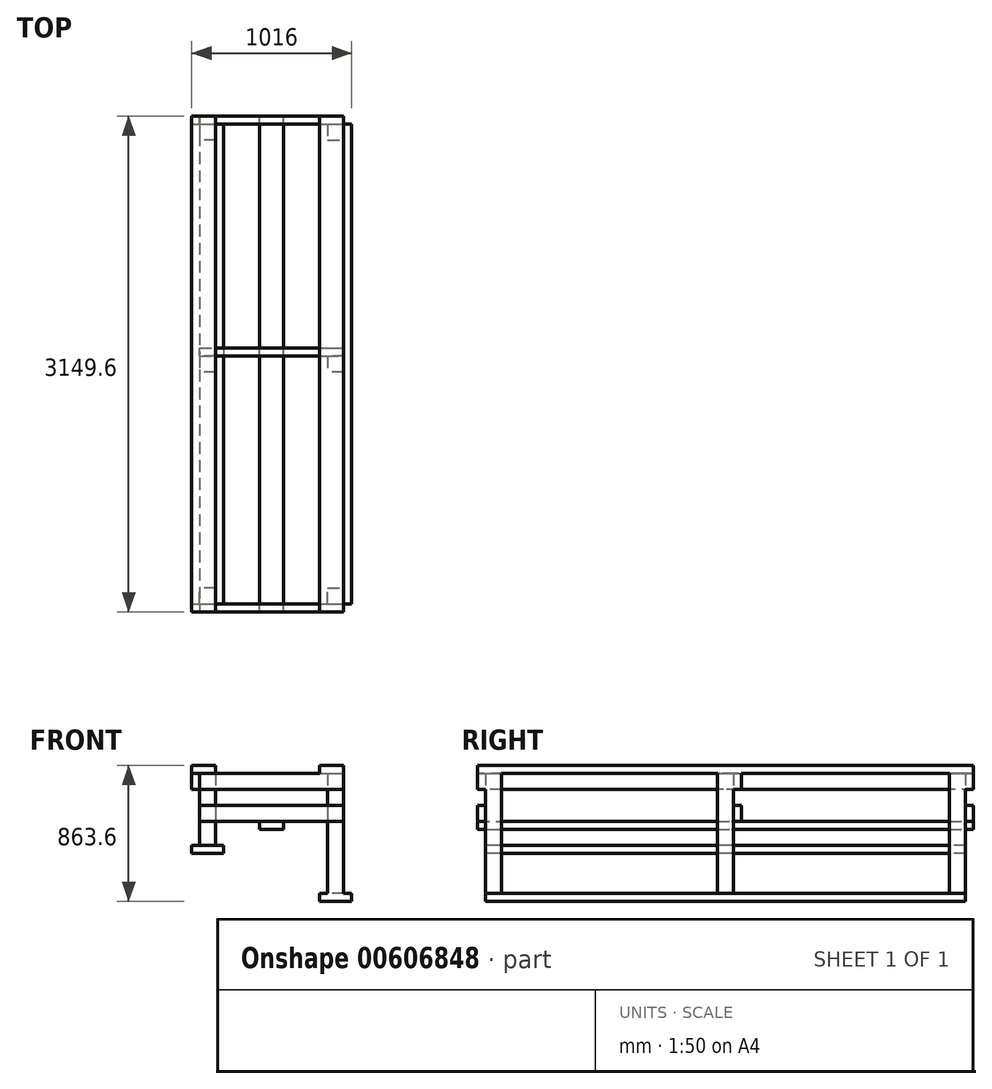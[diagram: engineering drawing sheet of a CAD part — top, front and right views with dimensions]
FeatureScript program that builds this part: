
annotation { "Feature Type Name" : "Feature", "Feature Type Description" : "" }
export const myFeature = defineFeature(function(context is Context, id is Id, definition is map)
    precondition{}
    {
        {
            var Q0;
            Q0=qCreatedBy(makeId("Front.planeOp"),FACE);
            var sketch = newSketch(context, id + "F0", { "sketchPlane" : qUnion([Q0])});
            skLineSegment(sketch, "E0.bottom", {"start": v(0, 0) * mm, "end": v(203.2, 0) * mm});
            skLineSegment(sketch, "E0.top", {"start": v(0, 50.8) * mm, "end": v(203.2, 50.8) * mm});
            skLineSegment(sketch, "E0.left", {"start": v(0, 0) * mm, "end": v(0, 50.8) * mm});
            skLineSegment(sketch, "E0.right", {"start": v(203.2, 0) * mm, "end": v(203.2, 50.8) * mm});
            skSolve(sketch);
        }
        {
            var Q0;
            Q0=makeQuery(id+"F0.imprint","IMPRINT",FACE,{"disambiguationData":[TD([[makeQuery(id+"F0.imprint","IMPRINT",EDGE,{"derivedFrom":sQuery(id+"F0.wireOp",EDGE,"E0.bottom")}),1.0]])]});
            extrude(context, id + "F1", {"entities" : qUnion([Q0]), "depth" : 3048 * mm, "offsetDistance" : 25.4 * mm});
        }
        {
            var Q0;
            Q0=makeQuery(id+"F1.opExtrude","SWEPT_FACE",FACE,{"disambiguationData":[OSD([sQuery(id+"F0.wireOp",EDGE,"E0.top")])]});
            var sketch = newSketch(context, id + "F2", { "sketchPlane" : qUnion([Q0])});
            skLineSegment(sketch, "E1", {"start": v(0, -3048) * mm, "end": v(50.8, -3048) * mm});
            skLineSegment(sketch, "E2.bottom", {"start": v(50.8, -3048) * mm, "end": v(152.4, -3048) * mm});
            skLineSegment(sketch, "E2.top", {"start": v(50.8, -2946.4) * mm, "end": v(152.4, -2946.4) * mm});
            skLineSegment(sketch, "E2.left", {"start": v(50.8, -3048) * mm, "end": v(50.8, -2946.4) * mm});
            skLineSegment(sketch, "E2.right", {"start": v(152.4, -3048) * mm, "end": v(152.4, -2946.4) * mm});
            skLineSegment(sketch, "E3", {"start": v(0, -3048) * mm, "end": v(0, -1524) * mm});
            skLineSegment(sketch, "E4", {"start": v(0, -1524) * mm, "end": v(203.2, -1524) * mm});
            skLineSegment(sketch, "E5.bottom", {"start": v(152.4, -1473.2) * mm, "end": v(50.8, -1473.2) * mm});
            skLineSegment(sketch, "E5.top", {"start": v(152.4, -1574.8) * mm, "end": v(50.8, -1574.8) * mm});
            skLineSegment(sketch, "E5.left", {"start": v(152.4, -1473.2) * mm, "end": v(152.4, -1574.8) * mm});
            skLineSegment(sketch, "E5.right", {"start": v(50.8, -1473.2) * mm, "end": v(50.8, -1574.8) * mm});
            skPoint(sketch, "E5.middle", {"position": v(101.6, -1524) * mm});
            skLineSegment(sketch, "E6", {"start": v(0, 0) * mm, "end": v(50.8, 0) * mm});
            skLineSegment(sketch, "E7.bottom", {"start": v(50.8, 0) * mm, "end": v(152.4, 0) * mm});
            skLineSegment(sketch, "E7.top", {"start": v(50.8, -101.6) * mm, "end": v(152.4, -101.6) * mm});
            skLineSegment(sketch, "E7.left", {"start": v(50.8, 0) * mm, "end": v(50.8, -101.6) * mm});
            skLineSegment(sketch, "E7.right", {"start": v(152.4, 0) * mm, "end": v(152.4, -101.6) * mm});
            skSolve(sketch);
        }
        {
            var Q0;
            Q0=makeQuery(id+"F2.imprint","IMPRINT",FACE,{"disambiguationData":[TD([[makeQuery(id+"F2.imprint","IMPRINT",EDGE,{"derivedFrom":sQuery(id+"F2.wireOp",EDGE,"E2.bottom")}),1.0]])]});
            var Q1;
            {var subQ5=sQuery(id+"F2.wireOp",EDGE,"E5.top");Q1=makeQuery(id+"F2.imprint","IMPRINT",FACE,{"disambiguationData":[TD([[makeQuery(id+"F2.imprint","IMPRINT",EDGE,{"derivedFrom":subQ5}),-1.0]])]});}
            var Q2;
            {var subQ5=sQuery(id+"F2.wireOp",EDGE,"E5.bottom");Q2=makeQuery(id+"F2.imprint","IMPRINT",FACE,{"disambiguationData":[TD([[makeQuery(id+"F2.imprint","IMPRINT",EDGE,{"derivedFrom":subQ5}),1.0]])]});}
            var Q3;
            Q3=makeQuery(id+"F2.imprint","IMPRINT",FACE,{"disambiguationData":[TD([[makeQuery(id+"F2.imprint","IMPRINT",EDGE,{"derivedFrom":sQuery(id+"F2.wireOp",EDGE,"E7.bottom")}),-1.0]])]});
            extrude(context, id + "F3", {"entities" : qUnion([Q0, Q1, Q2, Q3]), "operationType" : NewBodyOperationType.ADD, "depth" : 762 * mm, "offsetDistance" : 25.4 * mm});
        }
        {
            var Q0;
            Q0=makeQuery(id+"F3.opExtrude","SWEPT_FACE",FACE,{"disambiguationData":[OSD([sQuery(id+"F2.wireOp",EDGE,"E7.right")])]});
            var sketch = newSketch(context, id + "F4", { "sketchPlane" : qUnion([Q0])});
            skLineSegment(sketch, "E8.bottom", {"start": v(0, 812.8) * mm, "end": v(50.8, 812.8) * mm});
            skLineSegment(sketch, "E8.top", {"start": v(0, 711.2) * mm, "end": v(50.8, 711.2) * mm});
            skLineSegment(sketch, "E8.left", {"start": v(0, 812.8) * mm, "end": v(0, 711.2) * mm});
            skLineSegment(sketch, "E8.right", {"start": v(50.8, 812.8) * mm, "end": v(50.8, 711.2) * mm});
            skSolve(sketch);
        }
        {
            var Q0;
            Q0=makeQuery(id+"F4.imprint","IMPRINT",FACE,{"disambiguationData":[TD([[makeQuery(id+"F4.imprint","IMPRINT",EDGE,{"derivedFrom":sQuery(id+"F4.wireOp",EDGE,"E8.bottom")}),-1.0]])]});
            extrude(context, id + "F5", {"entities" : qUnion([Q0]), "operationType" : NewBodyOperationType.ADD, "oppositeDirection" : true, "depth" : 914.4 * mm, "offsetDistance" : 25.4 * mm});
        }
        {
            var Q0;
            Q0=makeQuery(id+"F3.opExtrude","SWEPT_FACE",FACE,{"disambiguationData":[OSD([sQuery(id+"F2.wireOp",EDGE,"E2.right")])]});
            var sketch = newSketch(context, id + "F6", { "sketchPlane" : qUnion([Q0])});
            skLineSegment(sketch, "E9.bottom", {"start": v(-3048, 812.8) * mm, "end": v(-3098.8, 812.8) * mm});
            skLineSegment(sketch, "E9.top", {"start": v(-3048, 711.2) * mm, "end": v(-3098.8, 711.2) * mm});
            skLineSegment(sketch, "E9.left", {"start": v(-3048, 812.8) * mm, "end": v(-3048, 711.2) * mm});
            skLineSegment(sketch, "E9.right", {"start": v(-3098.8, 812.8) * mm, "end": v(-3098.8, 711.2) * mm});
            skSolve(sketch);
        }
        {
            var Q0;
            Q0=makeQuery(id+"F6.imprint","IMPRINT",FACE,{"disambiguationData":[TD([[makeQuery(id+"F6.imprint","IMPRINT",EDGE,{"derivedFrom":sQuery(id+"F6.wireOp",EDGE,"E9.bottom")}),1.0]])]});
            extrude(context, id + "F7", {"entities" : qUnion([Q0]), "operationType" : NewBodyOperationType.ADD, "oppositeDirection" : true, "depth" : 914.4 * mm, "offsetDistance" : 25.4 * mm});
        }
        {
            var Q0;
            Q0=makeQuery(id+"F3.opExtrude","SWEPT_FACE",FACE,{"disambiguationData":[OSD([sQuery(id+"F2.wireOp",EDGE,"E5.left")])]});
            var sketch = newSketch(context, id + "F8", { "sketchPlane" : qUnion([Q0])});
            skLineSegment(sketch, "E10.bottom", {"start": v(-1473.2, 812.8) * mm, "end": v(-1422.4, 812.8) * mm});
            skLineSegment(sketch, "E10.top", {"start": v(-1473.2, 711.2) * mm, "end": v(-1422.4, 711.2) * mm});
            skLineSegment(sketch, "E10.left", {"start": v(-1473.2, 812.8) * mm, "end": v(-1473.2, 711.2) * mm});
            skLineSegment(sketch, "E10.right", {"start": v(-1422.4, 812.8) * mm, "end": v(-1422.4, 711.2) * mm});
            skSolve(sketch);
        }
        {
            var Q0;
            Q0=makeQuery(id+"F8.imprint","IMPRINT",FACE,{"disambiguationData":[TD([[makeQuery(id+"F8.imprint","IMPRINT",EDGE,{"derivedFrom":sQuery(id+"F8.wireOp",EDGE,"E10.bottom")}),-1.0]])]});
            extrude(context, id + "F9", {"entities" : qUnion([Q0]), "operationType" : NewBodyOperationType.ADD, "oppositeDirection" : true, "depth" : 914.4 * mm, "offsetDistance" : 25.4 * mm});
        }
        {
            var Q0;
            Q0=makeQuery(id+"F7.opExtrude","CAP_FACE",FACE,{"disambiguationData":[OSD([sQuery(id+"F6.wireOp",EDGE,"E9.bottom"),sQuery(id+"F6.wireOp",EDGE,"E9.top"),sQuery(id+"F6.wireOp",EDGE,"E9.left"),sQuery(id+"F6.wireOp",EDGE,"E9.right")])],"isStart":false});
            var sketch = newSketch(context, id + "F10", { "sketchPlane" : qUnion([Q0])});
            skLineSegment(sketch, "E11.bottom", {"start": v(3048, 812.8) * mm, "end": v(2946.4, 812.8) * mm});
            skLineSegment(sketch, "E11.top", {"start": v(3048, 355.6) * mm, "end": v(2946.4, 355.6) * mm});
            skLineSegment(sketch, "E11.left", {"start": v(3048, 812.8) * mm, "end": v(3048, 355.6) * mm});
            skLineSegment(sketch, "E11.right", {"start": v(2946.4, 812.8) * mm, "end": v(2946.4, 355.6) * mm});
            skSolve(sketch);
        }
        {
            var Q0;
            Q0=makeQuery(id+"F5.opExtrude","CAP_FACE",FACE,{"disambiguationData":[OSD([sQuery(id+"F4.wireOp",EDGE,"E8.bottom"),sQuery(id+"F4.wireOp",EDGE,"E8.top"),sQuery(id+"F4.wireOp",EDGE,"E8.left"),sQuery(id+"F4.wireOp",EDGE,"E8.right")])],"isStart":false});
            var sketch = newSketch(context, id + "F11", { "sketchPlane" : qUnion([Q0])});
            skLineSegment(sketch, "E12.bottom", {"start": v(0, 812.8) * mm, "end": v(101.6, 812.8) * mm});
            skLineSegment(sketch, "E12.top", {"start": v(0, 355.6) * mm, "end": v(101.6, 355.6) * mm});
            skLineSegment(sketch, "E12.left", {"start": v(0, 812.8) * mm, "end": v(0, 355.6) * mm});
            skLineSegment(sketch, "E12.right", {"start": v(101.6, 812.8) * mm, "end": v(101.6, 355.6) * mm});
            skSolve(sketch);
        }
        {
            var Q0;
            Q0=makeQuery(id+"F9.opExtrude","CAP_FACE",FACE,{"disambiguationData":[OSD([sQuery(id+"F8.wireOp",EDGE,"E10.bottom"),sQuery(id+"F8.wireOp",EDGE,"E10.top"),sQuery(id+"F8.wireOp",EDGE,"E10.left"),sQuery(id+"F8.wireOp",EDGE,"E10.right")])],"isStart":false});
            var sketch = newSketch(context, id + "F12", { "sketchPlane" : qUnion([Q0])});
            skLineSegment(sketch, "E13.bottom", {"start": v(1473.2, 812.8) * mm, "end": v(1574.8, 812.8) * mm});
            skLineSegment(sketch, "E13.top", {"start": v(1473.2, 355.6) * mm, "end": v(1574.8, 355.6) * mm});
            skLineSegment(sketch, "E13.left", {"start": v(1473.2, 812.8) * mm, "end": v(1473.2, 355.6) * mm});
            skLineSegment(sketch, "E13.right", {"start": v(1574.8, 812.8) * mm, "end": v(1574.8, 355.6) * mm});
            skSolve(sketch);
        }
        {
            var Q0;
            {var subQ1=sQuery(id+"F10.wireOp",EDGE,"E11.bottom");Q0=makeQuery(id+"F10.imprint","IMPRINT",FACE,{"disambiguationData":[TD([[makeQuery(id+"F10.imprint","IMPRINT",EDGE,{"derivedFrom":subQ1}),1.0]])]});}
            var Q1;
            {var subQ1=sQuery(id+"F12.wireOp",EDGE,"E13.bottom");Q1=makeQuery(id+"F12.imprint","IMPRINT",FACE,{"disambiguationData":[TD([[makeQuery(id+"F12.imprint","IMPRINT",EDGE,{"derivedFrom":subQ1}),-1.0]])]});}
            var Q2;
            {var subQ1=sQuery(id+"F11.wireOp",EDGE,"E12.bottom");Q2=makeQuery(id+"F11.imprint","IMPRINT",FACE,{"disambiguationData":[TD([[makeQuery(id+"F11.imprint","IMPRINT",EDGE,{"derivedFrom":subQ1}),-1.0]])]});}
            extrude(context, id + "F13", {"entities" : qUnion([Q0, Q1, Q2]), "oppositeDirection" : true, "depth" : 101.6 * mm, "offsetDistance" : 25.4 * mm});
        }
        {
            var Q0;
            Q0=makeQuery(id+"F7.opExtrude","SWEPT_FACE",FACE,{"disambiguationData":[OSD([sQuery(id+"F6.wireOp",EDGE,"E9.right")])]});
            var sketch = newSketch(context, id + "F14", { "sketchPlane" : qUnion([Q0])});
            skLineSegment(sketch, "E14.bottom", {"start": v(-762, 812.8) * mm, "end": v(-812.8, 812.8) * mm});
            skLineSegment(sketch, "E14.top", {"start": v(-762, 711.2) * mm, "end": v(-812.8, 711.2) * mm});
            skLineSegment(sketch, "E14.left", {"start": v(-762, 812.8) * mm, "end": v(-762, 711.2) * mm});
            skLineSegment(sketch, "E14.right", {"start": v(-812.8, 812.8) * mm, "end": v(-812.8, 711.2) * mm});
            skSolve(sketch);
        }
        {
            var Q0;
            Q0=makeQuery(id+"F14.imprint","IMPRINT",FACE,{"disambiguationData":[TD([[makeQuery(id+"F14.imprint","IMPRINT",EDGE,{"derivedFrom":sQuery(id+"F14.wireOp",EDGE,"E14.bottom")}),1.0]])]});
            extrude(context, id + "F15", {"entities" : qUnion([Q0]), "oppositeDirection" : true, "depth" : 3149.6 * mm, "offsetDistance" : 25.4 * mm});
        }
        {
            var Q0;
            Q0=makeQuery(id+"F13.opExtrude","SWEPT_FACE",FACE,{"disambiguationData":[OSD([sQuery(id+"F10.wireOp",EDGE,"E11.left")])]});
            var sketch = newSketch(context, id + "F16", { "sketchPlane" : qUnion([Q0])});
            skLineSegment(sketch, "E15", {"start": v(-660.4, 355.6) * mm, "end": v(-609.6, 355.6) * mm});
            skLineSegment(sketch, "E16.bottom", {"start": v(-609.6, 355.6) * mm, "end": v(-812.8, 355.6) * mm});
            skLineSegment(sketch, "E16.top", {"start": v(-609.6, 304.8) * mm, "end": v(-812.8, 304.8) * mm});
            skLineSegment(sketch, "E16.left", {"start": v(-609.6, 355.6) * mm, "end": v(-609.6, 304.8) * mm});
            skLineSegment(sketch, "E16.right", {"start": v(-812.8, 355.6) * mm, "end": v(-812.8, 304.8) * mm});
            skSolve(sketch);
        }
        {
            var Q0;
            Q0=makeQuery(id+"F16.imprint","IMPRINT",FACE,{"disambiguationData":[TD([[makeQuery(id+"F16.imprint","IMPRINT",EDGE,{"derivedFrom":sQuery(id+"F16.wireOp",EDGE,"E16.top")}),-1.0]])]});
            extrude(context, id + "F17", {"entities" : qUnion([Q0]), "oppositeDirection" : true, "depth" : 3048 * mm, "offsetDistance" : 25.4 * mm});
        }
        {
            var Q0;
            Q0=makeQuery(id+"F5.boolean.opBoolean","MERGE",FACE,{"derivedFrom":[makeQuery(id+"F3.opExtrude","SWEPT_FACE",FACE,{"disambiguationData":[OSD([sQuery(id+"F2.wireOp",EDGE,"E7.right")])]}),makeQuery(id+"F5.opExtrude","CAP_FACE",FACE,{"disambiguationData":[OSD([sQuery(id+"F4.wireOp",EDGE,"E8.bottom"),sQuery(id+"F4.wireOp",EDGE,"E8.top"),sQuery(id+"F4.wireOp",EDGE,"E8.left"),sQuery(id+"F4.wireOp",EDGE,"E8.right")])],"isStart":true})]});
            var sketch = newSketch(context, id + "F18", { "sketchPlane" : qUnion([Q0])});
            skLineSegment(sketch, "E17", {"start": v(0, 711.2) * mm, "end": v(0, 609.6) * mm});
            skLineSegment(sketch, "E18.bottom", {"start": v(0, 609.6) * mm, "end": v(50.8, 609.6) * mm});
            skLineSegment(sketch, "E18.top", {"start": v(0, 508) * mm, "end": v(50.8, 508) * mm});
            skLineSegment(sketch, "E18.left", {"start": v(0, 609.6) * mm, "end": v(0, 508) * mm});
            skLineSegment(sketch, "E18.right", {"start": v(50.8, 609.6) * mm, "end": v(50.8, 508) * mm});
            skSolve(sketch);
        }
        {
            var Q0;
            Q0=makeQuery(id+"F18.imprint","IMPRINT",FACE,{"disambiguationData":[TD([[makeQuery(id+"F18.imprint","IMPRINT",EDGE,{"derivedFrom":sQuery(id+"F18.wireOp",EDGE,"E18.bottom")}),-1.0]])]});
            extrude(context, id + "F19", {"entities" : qUnion([Q0]), "oppositeDirection" : true, "depth" : 914.4 * mm, "offsetDistance" : 25.4 * mm});
        }
        {
            var Q0;
            Q0=makeQuery(id+"F9.boolean.opBoolean","MERGE",FACE,{"derivedFrom":[makeQuery(id+"F3.opExtrude","SWEPT_FACE",FACE,{"disambiguationData":[OSD([sQuery(id+"F2.wireOp",EDGE,"E5.left")])]}),makeQuery(id+"F9.opExtrude","CAP_FACE",FACE,{"disambiguationData":[OSD([sQuery(id+"F8.wireOp",EDGE,"E10.bottom"),sQuery(id+"F8.wireOp",EDGE,"E10.top"),sQuery(id+"F8.wireOp",EDGE,"E10.left"),sQuery(id+"F8.wireOp",EDGE,"E10.right")])],"isStart":true})]});
            var sketch = newSketch(context, id + "F20", { "sketchPlane" : qUnion([Q0])});
            skLineSegment(sketch, "E19", {"start": v(-1473.2, 711.2) * mm, "end": v(-1473.2, 609.6) * mm});
            skLineSegment(sketch, "E20.bottom", {"start": v(-1473.2, 609.6) * mm, "end": v(-1422.4, 609.6) * mm});
            skLineSegment(sketch, "E20.top", {"start": v(-1473.2, 508) * mm, "end": v(-1422.4, 508) * mm});
            skLineSegment(sketch, "E20.left", {"start": v(-1473.2, 609.6) * mm, "end": v(-1473.2, 508) * mm});
            skLineSegment(sketch, "E20.right", {"start": v(-1422.4, 609.6) * mm, "end": v(-1422.4, 508) * mm});
            skSolve(sketch);
        }
        {
            var Q0;
            Q0=makeQuery(id+"F20.imprint","IMPRINT",FACE,{"disambiguationData":[TD([[makeQuery(id+"F20.imprint","IMPRINT",EDGE,{"derivedFrom":sQuery(id+"F20.wireOp",EDGE,"E20.bottom")}),-1.0]])]});
            extrude(context, id + "F21", {"entities" : qUnion([Q0]), "oppositeDirection" : true, "depth" : 914.4 * mm, "offsetDistance" : 25.4 * mm});
        }
        {
            var Q0;
            Q0=makeQuery(id+"F7.boolean.opBoolean","MERGE",FACE,{"derivedFrom":[makeQuery(id+"F3.opExtrude","SWEPT_FACE",FACE,{"disambiguationData":[OSD([sQuery(id+"F2.wireOp",EDGE,"E2.right")])]}),makeQuery(id+"F7.opExtrude","CAP_FACE",FACE,{"disambiguationData":[OSD([sQuery(id+"F6.wireOp",EDGE,"E9.bottom"),sQuery(id+"F6.wireOp",EDGE,"E9.top"),sQuery(id+"F6.wireOp",EDGE,"E9.left"),sQuery(id+"F6.wireOp",EDGE,"E9.right")])],"isStart":true})]});
            var sketch = newSketch(context, id + "F22", { "sketchPlane" : qUnion([Q0])});
            skLineSegment(sketch, "E21", {"start": v(-3048, 711.2) * mm, "end": v(-3048, 609.6) * mm});
            skLineSegment(sketch, "E22.bottom", {"start": v(-3048, 609.6) * mm, "end": v(-3098.8, 609.6) * mm});
            skLineSegment(sketch, "E22.top", {"start": v(-3048, 508) * mm, "end": v(-3098.8, 508) * mm});
            skLineSegment(sketch, "E22.left", {"start": v(-3048, 609.6) * mm, "end": v(-3048, 508) * mm});
            skLineSegment(sketch, "E22.right", {"start": v(-3098.8, 609.6) * mm, "end": v(-3098.8, 508) * mm});
            skSolve(sketch);
        }
        {
            var Q0;
            Q0=makeQuery(id+"F22.imprint","IMPRINT",FACE,{"disambiguationData":[TD([[makeQuery(id+"F22.imprint","IMPRINT",EDGE,{"derivedFrom":sQuery(id+"F22.wireOp",EDGE,"E22.bottom")}),1.0]])]});
            extrude(context, id + "F23", {"entities" : qUnion([Q0]), "oppositeDirection" : true, "depth" : 914.4 * mm, "offsetDistance" : 25.4 * mm});
        }
        {
            var Q0;
            Q0=makeQuery(id+"F5.opExtrude","SWEPT_FACE",FACE,{"disambiguationData":[OSD([sQuery(id+"F4.wireOp",EDGE,"E8.right")])]});
            var sketch = newSketch(context, id + "F24", { "sketchPlane" : qUnion([Q0])});
            skLineSegment(sketch, "E23.bottom", {"start": v(-152.4, 812.8) * mm, "end": v(0, 812.8) * mm});
            skLineSegment(sketch, "E23.top", {"start": v(-152.4, 863.6) * mm, "end": v(0, 863.6) * mm});
            skLineSegment(sketch, "E23.left", {"start": v(-152.4, 812.8) * mm, "end": v(-152.4, 863.6) * mm});
            skLineSegment(sketch, "E23.right", {"start": v(0, 812.8) * mm, "end": v(0, 863.6) * mm});
            skSolve(sketch);
        }
        {
            var Q0;
            Q0 = qSketchRegion(id + "F24", true);
            extrude(context, id + "F25", {"entities" : qUnion([Q0]), "operationType" : NewBodyOperationType.ADD, "oppositeDirection" : true, "depth" : 3149.6 * mm, "offsetDistance" : 25.4 * mm});
        }
        {
            var Q0;
            Q0=makeQuery(id+"F15.opExtrude","CAP_FACE",FACE,{"disambiguationData":[OSD([sQuery(id+"F14.wireOp",EDGE,"E14.bottom"),sQuery(id+"F14.wireOp",EDGE,"E14.top"),sQuery(id+"F14.wireOp",EDGE,"E14.left"),sQuery(id+"F14.wireOp",EDGE,"E14.right")])],"isStart":false});
            var sketch = newSketch(context, id + "F26", { "sketchPlane" : qUnion([Q0])});
            skLineSegment(sketch, "E24.bottom", {"start": v(812.8, 812.8) * mm, "end": v(660.4, 812.8) * mm});
            skLineSegment(sketch, "E24.top", {"start": v(812.8, 863.6) * mm, "end": v(660.4, 863.6) * mm});
            skLineSegment(sketch, "E24.left", {"start": v(812.8, 812.8) * mm, "end": v(812.8, 863.6) * mm});
            skLineSegment(sketch, "E24.right", {"start": v(660.4, 812.8) * mm, "end": v(660.4, 863.6) * mm});
            skSolve(sketch);
        }
        {
            var Q0;
            Q0=makeQuery(id+"F26.imprint","IMPRINT",FACE,{"disambiguationData":[TD([[makeQuery(id+"F26.imprint","IMPRINT",EDGE,{"derivedFrom":sQuery(id+"F26.wireOp",EDGE,"E24.top")}),1.0]])]});
            extrude(context, id + "F27", {"entities" : qUnion([Q0]), "oppositeDirection" : true, "depth" : 3149.6 * mm, "offsetDistance" : 25.4 * mm});
        }
        {
            var Q0;
            Q0=makeQuery(id+"F19.opExtrude","SWEPT_FACE",FACE,{"disambiguationData":[OSD([sQuery(id+"F18.wireOp",EDGE,"E18.right")])]});
            var sketch = newSketch(context, id + "F28", { "sketchPlane" : qUnion([Q0])});
            skLineSegment(sketch, "E25", {"start": v(-152.4, 508) * mm, "end": v(304.8, 508) * mm});
            skLineSegment(sketch, "E26", {"start": v(304.8, 508) * mm, "end": v(228.6, 508) * mm});
            skLineSegment(sketch, "E27.bottom", {"start": v(228.6, 508) * mm, "end": v(381, 508) * mm});
            skLineSegment(sketch, "E27.top", {"start": v(228.6, 457.2) * mm, "end": v(381, 457.2) * mm});
            skLineSegment(sketch, "E27.left", {"start": v(228.6, 508) * mm, "end": v(228.6, 457.2) * mm});
            skLineSegment(sketch, "E27.right", {"start": v(381, 508) * mm, "end": v(381, 457.2) * mm});
            skSolve(sketch);
        }
        {
            var Q0;
            Q0=makeQuery(id+"F28.imprint","IMPRINT",FACE,{"disambiguationData":[TD([[makeQuery(id+"F28.imprint","IMPRINT",EDGE,{"derivedFrom":sQuery(id+"F28.wireOp",EDGE,"E27.top")}),1.0]])]});
            extrude(context, id + "F29", {"entities" : qUnion([Q0]), "oppositeDirection" : true, "depth" : 3149.6 * mm, "offsetDistance" : 25.4 * mm});
        }
    });
